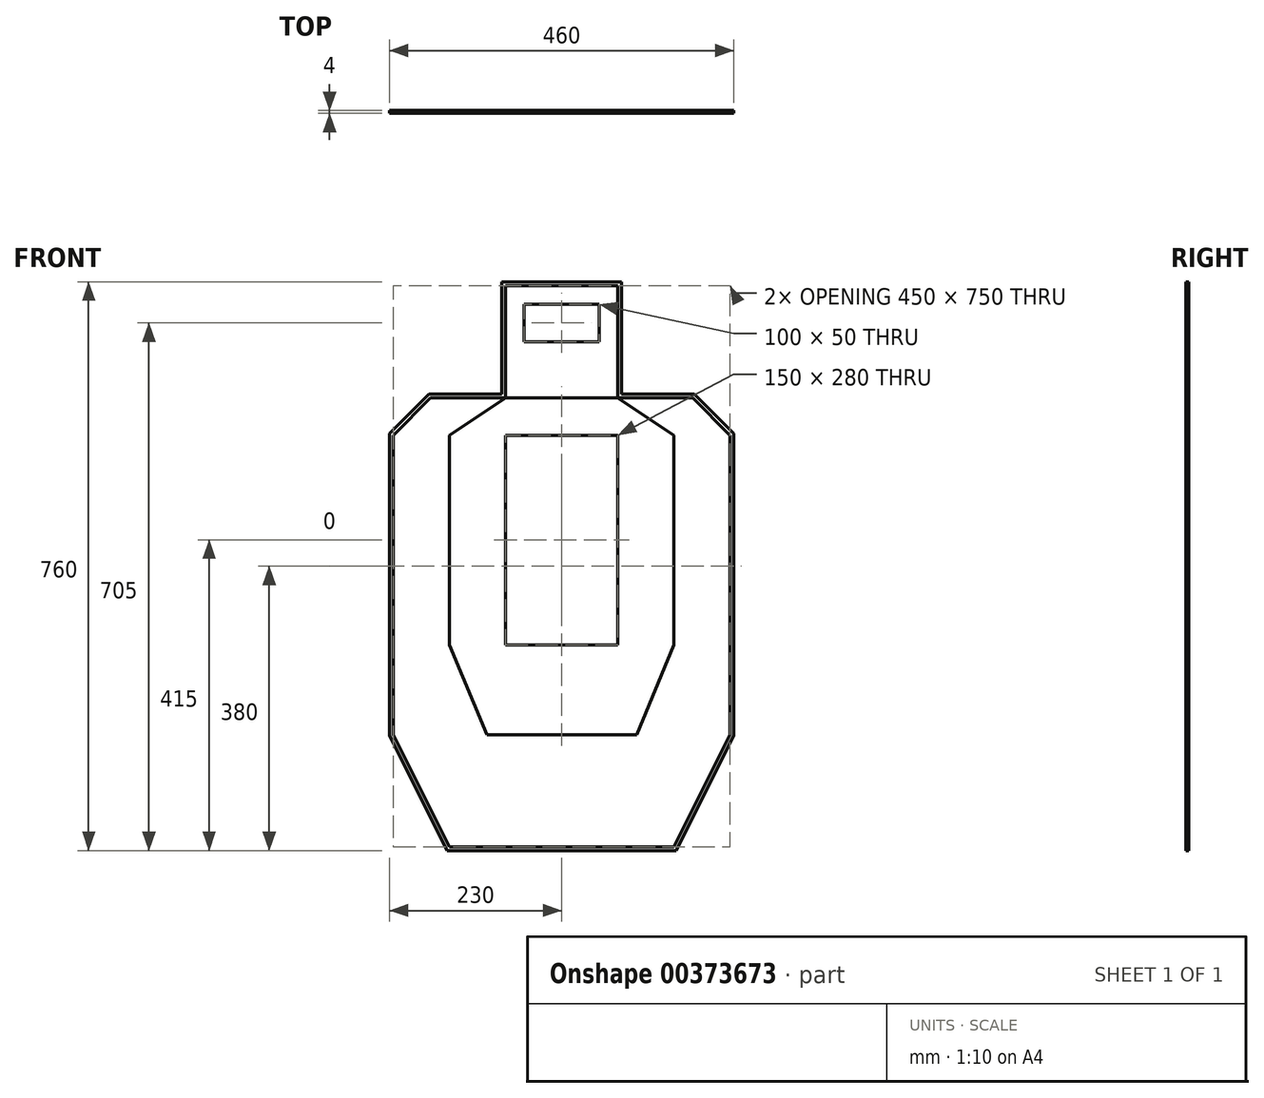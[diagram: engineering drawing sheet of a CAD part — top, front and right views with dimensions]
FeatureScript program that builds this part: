
annotation { "Feature Type Name" : "Feature", "Feature Type Description" : "" }
export const myFeature = defineFeature(function(context is Context, id is Id, definition is map)
    precondition{}
    {
        {
            var Q0;
            Q0=qCreatedBy(makeId("Front.planeOp"),FACE);
            var sketch = newSketch(context, id + "F0", { "sketchPlane" : qUnion([Q0])});
            skLineSegment(sketch, "E0.bottom", {"start": v(0, 100) * mm, "end": v(50, 100) * mm, "construction": true});
            skLineSegment(sketch, "E0.top", {"start": v(0, 125) * mm, "end": v(50, 125) * mm});
            skLineSegment(sketch, "E0.right", {"start": v(50, 100) * mm, "end": v(50, 125) * mm});
            skLineSegment(sketch, "E1.MirrorCS", {"start": v(0, 75) * mm, "end": v(50, 75) * mm});
            skLineSegment(sketch, "E2.MirrorCS", {"start": v(50, 100) * mm, "end": v(50, 75) * mm});
            skLineSegment(sketch, "E3.MirrorCS", {"start": v(0, 0) * mm, "end": v(0, 100) * mm, "construction": true});
            skLineSegment(sketch, "E4.MirrorCS", {"start": v(0, 125) * mm, "end": v(-50, 125) * mm});
            skLineSegment(sketch, "E5.MirrorCS", {"start": v(-50, 100) * mm, "end": v(-50, 125) * mm});
            skLineSegment(sketch, "E6.MirrorCS", {"start": v(-50, 100) * mm, "end": v(-50, 75) * mm});
            skLineSegment(sketch, "E7.MirrorCS", {"start": v(0, 75) * mm, "end": v(-50, 75) * mm});
            skSolve(sketch);
        }
        {
            var Q0;
            Q0 = qSketchRegion(id + "F0", true);
            extrude(context, id + "F1", {"entities" : qUnion([Q0]), "oppositeDirection" : true, "depth" : 3 * mm});
        }
        {
            var Q0;
            Q0=qCreatedBy(makeId("Front.planeOp"),FACE);
            var sketch = newSketch(context, id + "F2", { "sketchPlane" : qUnion([Q0])});
            skLineSegment(sketch, "E8", {"start": v(75, 0) * mm, "end": v(75, 150) * mm});
            skLineSegment(sketch, "E9", {"start": v(75, 150) * mm, "end": v(-75, 150) * mm});
            skLineSegment(sketch, "E10", {"start": v(-75, 150) * mm, "end": v(-75, 0) * mm});
            skLineSegment(sketch, "E11", {"start": v(-75, 0) * mm, "end": v(75, 0) * mm});
            skLineSegment(sketch, "E12.0", {"start": v(0, 125) * mm, "end": v(-50, 125) * mm});
            skLineSegment(sketch, "E13.0", {"start": v(0, 125) * mm, "end": v(50, 125) * mm});
            skLineSegment(sketch, "E14.0", {"start": v(50, 100) * mm, "end": v(50, 125) * mm});
            skLineSegment(sketch, "E15.1", {"start": v(50, 100) * mm, "end": v(50, 75) * mm});
            skLineSegment(sketch, "E16.0", {"start": v(0, 75) * mm, "end": v(50, 75) * mm});
            skLineSegment(sketch, "E17.0", {"start": v(0, 75) * mm, "end": v(-50, 75) * mm});
            skLineSegment(sketch, "E18.0", {"start": v(-50, 100) * mm, "end": v(-50, 75) * mm});
            skLineSegment(sketch, "E19.1", {"start": v(-50, 100) * mm, "end": v(-50, 125) * mm});
            skLineSegment(sketch, "E20", {"start": v(0, 125) * mm, "end": v(0, 150) * mm, "construction": true});
            skLineSegment(sketch, "E21", {"start": v(0, 150) * mm, "end": v(0, 137.5) * mm, "construction": true});
            skSolve(sketch);
        }
        {
            var Q0;
            {var subQ0=sQuery(id+"F2.wireOp",EDGE,"E8");Q0=makeQuery(id+"F2.imprint","IMPRINT",FACE,{"disambiguationData":[TD([[makeQuery(id+"F2.imprint","IMPRINT",EDGE,{"derivedFrom":subQ0}),1.0]])]});}
            extrude(context, id + "F3", {"entities" : qUnion([Q0]), "oppositeDirection" : true, "depth" : 3 * mm});
        }
        {
            var Q0;
            Q0=qCreatedBy(makeId("Front.planeOp"),FACE);
            var sketch = newSketch(context, id + "F4", { "sketchPlane" : qUnion([Q0])});
            skLineSegment(sketch, "E22.bottom", {"start": v(75, -50) * mm, "end": v(-75, -50) * mm});
            skLineSegment(sketch, "E22.top", {"start": v(75, -330) * mm, "end": v(-75, -330) * mm});
            skLineSegment(sketch, "E22.left", {"start": v(75, -50) * mm, "end": v(75, -330) * mm});
            skLineSegment(sketch, "E22.right", {"start": v(-75, -50) * mm, "end": v(-75, -330) * mm});
            skLineSegment(sketch, "E23", {"start": v(0, 0) * mm, "end": v(0, -50) * mm, "construction": true});
            skLineSegment(sketch, "E24.0", {"start": v(-75, 0) * mm, "end": v(75, 0) * mm, "construction": true});
            skLineSegment(sketch, "E25", {"start": v(75, 0) * mm, "end": v(75, -50) * mm, "construction": true});
            skSolve(sketch);
        }
        {
            var Q0;
            Q0=makeQuery(id+"F4.imprint","IMPRINT",FACE,{"disambiguationData":[TD([[makeQuery(id+"F4.imprint","IMPRINT",EDGE,{"derivedFrom":sQuery(id+"F4.wireOp",EDGE,"E22.bottom")}),1.0]])]});
            extrude(context, id + "F5", {"entities" : qUnion([Q0]), "oppositeDirection" : true, "depth" : 3 * mm});
        }
        {
            var Q0;
            Q0=qCreatedBy(makeId("Front.planeOp"),FACE);
            var sketch = newSketch(context, id + "F6", { "sketchPlane" : qUnion([Q0])});
            skLineSegment(sketch, "E26.0", {"start": v(-75, 0) * mm, "end": v(75, 0) * mm});
            skLineSegment(sketch, "E27.1", {"start": v(75, -50) * mm, "end": v(75, -330) * mm});
            skLineSegment(sketch, "E28.2", {"start": v(75, -50) * mm, "end": v(-75, -50) * mm});
            skLineSegment(sketch, "E29.3", {"start": v(-75, -50) * mm, "end": v(-75, -330) * mm});
            skLineSegment(sketch, "E30.0", {"start": v(75, -330) * mm, "end": v(-75, -330) * mm});
            skLineSegment(sketch, "E31", {"start": v(75, 0) * mm, "end": v(150, -50) * mm});
            skLineSegment(sketch, "E32", {"start": v(150, -50) * mm, "end": v(150, -330) * mm});
            skLineSegment(sketch, "E33", {"start": v(150, -330) * mm, "end": v(100, -450) * mm});
            skLineSegment(sketch, "E34", {"start": v(100, -450) * mm, "end": v(-100, -450) * mm});
            skLineSegment(sketch, "E35", {"start": v(-100, -450) * mm, "end": v(-150, -330) * mm});
            skLineSegment(sketch, "E36", {"start": v(-150, -330) * mm, "end": v(-150, -50) * mm});
            skLineSegment(sketch, "E37", {"start": v(-150, -50) * mm, "end": v(-75, 0) * mm});
            skLineSegment(sketch, "E38", {"start": v(0, -450) * mm, "end": v(0, -50) * mm, "construction": true});
            skLineSegment(sketch, "E39", {"start": v(150, -50) * mm, "end": v(75, -50) * mm, "construction": true});
            skLineSegment(sketch, "E40", {"start": v(-55.04, -50) * mm, "end": v(-150, -50) * mm, "construction": true});
            skLineSegment(sketch, "E41", {"start": v(150, -330) * mm, "end": v(150, -450) * mm, "construction": true});
            skLineSegment(sketch, "E42", {"start": v(100, -450) * mm, "end": v(150, -450) * mm, "construction": true});
            skLineSegment(sketch, "E43", {"start": v(150, -330) * mm, "end": v(-150, -330) * mm, "construction": true});
            skLineSegment(sketch, "E44", {"start": v(-150, -330) * mm, "end": v(-150, -450) * mm, "construction": true});
            skLineSegment(sketch, "E45", {"start": v(-150, -450) * mm, "end": v(-100, -450) * mm, "construction": true});
            skSolve(sketch);
        }
        {
            var Q0;
            Q0=makeQuery(id+"F6.imprint","IMPRINT",FACE,{"disambiguationData":[TD([[makeQuery(id+"F6.imprint","IMPRINT",EDGE,{"derivedFrom":sQuery(id+"F6.wireOp",EDGE,"E26.0")}),-1.0]])]});
            extrude(context, id + "F7", {"entities" : qUnion([Q0]), "oppositeDirection" : true, "depth" : 3 * mm});
        }
        {
            var Q0;
            Q0=makeQuery(id+"F7.opExtrude","CAP_FACE",FACE,{"disambiguationData":[OSD([sQuery(id+"F6.wireOp",EDGE,"E26.0"),sQuery(id+"F6.wireOp",EDGE,"E27.1"),sQuery(id+"F6.wireOp",EDGE,"E28.2"),sQuery(id+"F6.wireOp",EDGE,"E29.3"),sQuery(id+"F6.wireOp",EDGE,"E30.0"),sQuery(id+"F6.wireOp",EDGE,"E31"),sQuery(id+"F6.wireOp",EDGE,"E32"),sQuery(id+"F6.wireOp",EDGE,"E33"),sQuery(id+"F6.wireOp",EDGE,"E34"),sQuery(id+"F6.wireOp",EDGE,"E35"),sQuery(id+"F6.wireOp",EDGE,"E36"),sQuery(id+"F6.wireOp",EDGE,"E37")])],"isStart":true});
            var sketch = newSketch(context, id + "F8", { "sketchPlane" : qUnion([Q0])});
            skLineSegment(sketch, "E46.0", {"start": v(75, 0) * mm, "end": v(150, -50) * mm});
            skLineSegment(sketch, "E47.0", {"start": v(150, -50) * mm, "end": v(150, -330) * mm});
            skLineSegment(sketch, "E48.0", {"start": v(150, -330) * mm, "end": v(100, -450) * mm});
            skLineSegment(sketch, "E49.1", {"start": v(100, -450) * mm, "end": v(-100, -450) * mm});
            skLineSegment(sketch, "E50.0", {"start": v(-150, -330) * mm, "end": v(-150, -50) * mm});
            skLineSegment(sketch, "E51.0", {"start": v(-100, -450) * mm, "end": v(-150, -330) * mm});
            skLineSegment(sketch, "E52.0", {"start": v(-150, -50) * mm, "end": v(-75, 0) * mm});
            skLineSegment(sketch, "E53", {"start": v(75, 0) * mm, "end": v(175, 0) * mm});
            skLineSegment(sketch, "E54", {"start": v(175, 0) * mm, "end": v(225, -50) * mm});
            skLineSegment(sketch, "E55", {"start": v(225, -50) * mm, "end": v(225, -450) * mm});
            skLineSegment(sketch, "E56", {"start": v(225, -450) * mm, "end": v(150, -600) * mm});
            skLineSegment(sketch, "E57", {"start": v(150, -600) * mm, "end": v(-150, -600) * mm});
            skLineSegment(sketch, "E58", {"start": v(-150, -600) * mm, "end": v(-225, -450) * mm});
            skLineSegment(sketch, "E59", {"start": v(-225, -450) * mm, "end": v(-225, -50) * mm});
            skLineSegment(sketch, "E60", {"start": v(-225, -50) * mm, "end": v(-175, 0) * mm});
            skLineSegment(sketch, "E61", {"start": v(-175, 0) * mm, "end": v(-75, 0) * mm});
            skLineSegment(sketch, "E62", {"start": v(225, -50) * mm, "end": v(225, 0) * mm, "construction": true});
            skLineSegment(sketch, "E63", {"start": v(225, 0) * mm, "end": v(175, 0) * mm, "construction": true});
            skLineSegment(sketch, "E64", {"start": v(225, -450) * mm, "end": v(225, -600) * mm, "construction": true});
            skLineSegment(sketch, "E65", {"start": v(225, -600) * mm, "end": v(150, -600) * mm, "construction": true});
            skLineSegment(sketch, "E66", {"start": v(-225, -450) * mm, "end": v(-225, -600) * mm, "construction": true});
            skLineSegment(sketch, "E67", {"start": v(-225, -600) * mm, "end": v(-150, -600) * mm, "construction": true});
            skLineSegment(sketch, "E68", {"start": v(-175, 0) * mm, "end": v(-225, 0) * mm, "construction": true});
            skLineSegment(sketch, "E69", {"start": v(-225, 0) * mm, "end": v(-225, -50) * mm, "construction": true});
            skSolve(sketch);
        }
        {
            var Q0;
            Q0 = qSketchRegion(id + "F8", true);
            extrude(context, id + "F9", {"entities" : qUnion([Q0]), "oppositeDirection" : true, "depth" : 3 * mm});
        }
        {
            var Q0;
            Q0=makeQuery(id+"F9.opExtrude","CAP_FACE",FACE,{"disambiguationData":[OSD([sQuery(id+"F8.wireOp",EDGE,"E46.0"),sQuery(id+"F8.wireOp",EDGE,"E47.0"),sQuery(id+"F8.wireOp",EDGE,"E48.0"),sQuery(id+"F8.wireOp",EDGE,"E49.1"),sQuery(id+"F8.wireOp",EDGE,"E50.0"),sQuery(id+"F8.wireOp",EDGE,"E51.0"),sQuery(id+"F8.wireOp",EDGE,"E52.0"),sQuery(id+"F8.wireOp",EDGE,"E53"),sQuery(id+"F8.wireOp",EDGE,"E54"),sQuery(id+"F8.wireOp",EDGE,"E55"),sQuery(id+"F8.wireOp",EDGE,"E56"),sQuery(id+"F8.wireOp",EDGE,"E57"),sQuery(id+"F8.wireOp",EDGE,"E58"),sQuery(id+"F8.wireOp",EDGE,"E59"),sQuery(id+"F8.wireOp",EDGE,"E60"),sQuery(id+"F8.wireOp",EDGE,"E61")])],"isStart":true});
            var sketch = newSketch(context, id + "F10", { "sketchPlane" : qUnion([Q0])});
            skLineSegment(sketch, "E70.0", {"start": v(75, 150) * mm, "end": v(-75, 150) * mm});
            skLineSegment(sketch, "E71.0", {"start": v(75, 0) * mm, "end": v(75, 150) * mm});
            skLineSegment(sketch, "E72.1", {"start": v(75, 0) * mm, "end": v(175, 0) * mm});
            skLineSegment(sketch, "E73.0", {"start": v(175, 0) * mm, "end": v(225, -50) * mm});
            skLineSegment(sketch, "E74.1", {"start": v(225, -50) * mm, "end": v(225, -450) * mm});
            skLineSegment(sketch, "E75.0", {"start": v(225, -450) * mm, "end": v(150, -600) * mm});
            skLineSegment(sketch, "E76.1", {"start": v(150, -600) * mm, "end": v(-150, -600) * mm});
            skLineSegment(sketch, "E77.2", {"start": v(-150, -600) * mm, "end": v(-225, -450) * mm});
            skLineSegment(sketch, "E78.3", {"start": v(-225, -450) * mm, "end": v(-225, -50) * mm});
            skLineSegment(sketch, "E79.4", {"start": v(-225, -50) * mm, "end": v(-175, 0) * mm});
            skLineSegment(sketch, "E80.5", {"start": v(-175, 0) * mm, "end": v(-75, 0) * mm});
            skLineSegment(sketch, "E81.0", {"start": v(-75, 150) * mm, "end": v(-75, 0) * mm});
            skLineSegment(sketch, "E82.0", {"start": v(177.07, 5) * mm, "end": v(230, -47.93) * mm});
            skLineSegment(sketch, "E82.1", {"start": v(-230, -451.18) * mm, "end": v(-230, -47.93) * mm});
            skLineSegment(sketch, "E82.2", {"start": v(-153.1, -605) * mm, "end": v(-230, -451.18) * mm});
            skLineSegment(sketch, "E82.3", {"start": v(153.1, -605) * mm, "end": v(-153.1, -605) * mm});
            skLineSegment(sketch, "E82.4", {"start": v(230, -451.18) * mm, "end": v(153.1, -605) * mm});
            skLineSegment(sketch, "E82.5", {"start": v(-230, -47.93) * mm, "end": v(-177.07, 5) * mm});
            skLineSegment(sketch, "E82.6", {"start": v(230, -47.93) * mm, "end": v(230, -451.18) * mm});
            skLineSegment(sketch, "E82.7", {"start": v(-177.07, 5) * mm, "end": v(-80, 5) * mm});
            skLineSegment(sketch, "E82.8", {"start": v(-80, 155) * mm, "end": v(-80, 5) * mm});
            skLineSegment(sketch, "E82.9", {"start": v(80, 155) * mm, "end": v(-80, 155) * mm});
            skLineSegment(sketch, "E82.10", {"start": v(80, 5) * mm, "end": v(80, 155) * mm});
            skLineSegment(sketch, "E82.11", {"start": v(80, 5) * mm, "end": v(177.07, 5) * mm});
            skSolve(sketch);
        }
        {
            var Q0;
            Q0=makeQuery(id+"F10.imprint","IMPRINT",FACE,{"disambiguationData":[TD([[makeQuery(id+"F10.imprint","IMPRINT",EDGE,{"derivedFrom":sQuery(id+"F10.wireOp",EDGE,"E70.0")}),-1.0]])]});
            extrude(context, id + "F11", {"entities" : qUnion([Q0]), "oppositeDirection" : true, "depth" : 3 * mm});
        }
        {
            var Q0;
            Q0=makeQuery(id+"F9.opExtrude","CAP_FACE",FACE,{"disambiguationData":[OSD([sQuery(id+"F8.wireOp",EDGE,"E46.0"),sQuery(id+"F8.wireOp",EDGE,"E47.0"),sQuery(id+"F8.wireOp",EDGE,"E48.0"),sQuery(id+"F8.wireOp",EDGE,"E49.1"),sQuery(id+"F8.wireOp",EDGE,"E50.0"),sQuery(id+"F8.wireOp",EDGE,"E51.0"),sQuery(id+"F8.wireOp",EDGE,"E52.0"),sQuery(id+"F8.wireOp",EDGE,"E53"),sQuery(id+"F8.wireOp",EDGE,"E54"),sQuery(id+"F8.wireOp",EDGE,"E55"),sQuery(id+"F8.wireOp",EDGE,"E56"),sQuery(id+"F8.wireOp",EDGE,"E57"),sQuery(id+"F8.wireOp",EDGE,"E58"),sQuery(id+"F8.wireOp",EDGE,"E59"),sQuery(id+"F8.wireOp",EDGE,"E60"),sQuery(id+"F8.wireOp",EDGE,"E61")])],"isStart":false});
            var sketch = newSketch(context, id + "F12", { "sketchPlane" : qUnion([Q0])});
            skLineSegment(sketch, "E83.0", {"start": v(75, 150) * mm, "end": v(75, 0) * mm});
            skLineSegment(sketch, "E84.0", {"start": v(175, 0) * mm, "end": v(75, 0) * mm});
            skLineSegment(sketch, "E85.0", {"start": v(-75, 150) * mm, "end": v(75, 150) * mm});
            skLineSegment(sketch, "E86.0", {"start": v(225, -50) * mm, "end": v(175, 0) * mm});
            skLineSegment(sketch, "E87.0", {"start": v(-225, -50) * mm, "end": v(-225, -450) * mm});
            skLineSegment(sketch, "E87.1", {"start": v(225, -450) * mm, "end": v(225, -50) * mm});
            skLineSegment(sketch, "E87.2", {"start": v(150, -600) * mm, "end": v(225, -450) * mm});
            skLineSegment(sketch, "E87.3", {"start": v(-225, -450) * mm, "end": v(-150, -600) * mm});
            skLineSegment(sketch, "E87.4", {"start": v(-150, -600) * mm, "end": v(150, -600) * mm});
            skLineSegment(sketch, "E88.0", {"start": v(-175, 0) * mm, "end": v(-225, -50) * mm});
            skLineSegment(sketch, "E89.0", {"start": v(-75, 0) * mm, "end": v(-175, 0) * mm});
            skLineSegment(sketch, "E90.0", {"start": v(-75, 0) * mm, "end": v(-75, 150) * mm});
            skSolve(sketch);
        }
        {
            var Q0;
            Q0 = qSketchRegion(id + "F12", true);
            extrude(context, id + "F13", {"entities" : qUnion([Q0]), "depth" : 1 * mm});
        }
        {
            var Q0;
            Q0=makeQuery(id+"F13.opExtrude","CAP_FACE",FACE,{"disambiguationData":[OSD([sQuery(id+"F12.wireOp",EDGE,"E83.0"),sQuery(id+"F12.wireOp",EDGE,"E84.0"),sQuery(id+"F12.wireOp",EDGE,"E85.0"),sQuery(id+"F12.wireOp",EDGE,"E86.0"),sQuery(id+"F12.wireOp",EDGE,"E87.0"),sQuery(id+"F12.wireOp",EDGE,"E87.1"),sQuery(id+"F12.wireOp",EDGE,"E87.2"),sQuery(id+"F12.wireOp",EDGE,"E87.3"),sQuery(id+"F12.wireOp",EDGE,"E87.4"),sQuery(id+"F12.wireOp",EDGE,"E88.0"),sQuery(id+"F12.wireOp",EDGE,"E89.0"),sQuery(id+"F12.wireOp",EDGE,"E90.0")])],"isStart":false});
            var sketch = newSketch(context, id + "F14", { "sketchPlane" : qUnion([Q0])});
            skLineSegment(sketch, "E91.0", {"start": v(-80, 155) * mm, "end": v(80, 155) * mm});
            skLineSegment(sketch, "E92.0", {"start": v(80, 155) * mm, "end": v(80, 5) * mm});
            skLineSegment(sketch, "E93.0", {"start": v(-80, 5) * mm, "end": v(-80, 155) * mm});
            skLineSegment(sketch, "E94.0", {"start": v(177.07, 5) * mm, "end": v(80, 5) * mm});
            skLineSegment(sketch, "E95.0", {"start": v(-80, 5) * mm, "end": v(-177.07, 5) * mm});
            skLineSegment(sketch, "E96.0", {"start": v(230, -47.93) * mm, "end": v(177.07, 5) * mm});
            skLineSegment(sketch, "E97.0", {"start": v(-177.07, 5) * mm, "end": v(-230, -47.93) * mm});
            skLineSegment(sketch, "E98.1", {"start": v(-230, -47.93) * mm, "end": v(-230, -451.18) * mm});
            skLineSegment(sketch, "E99.0", {"start": v(-230, -451.18) * mm, "end": v(-153.1, -605) * mm});
            skLineSegment(sketch, "E100.0", {"start": v(-153.1, -605) * mm, "end": v(153.1, -605) * mm});
            skLineSegment(sketch, "E101.0", {"start": v(153.1, -605) * mm, "end": v(230, -451.18) * mm});
            skLineSegment(sketch, "E102.0", {"start": v(230, -451.18) * mm, "end": v(230, -47.93) * mm});
            skLineSegment(sketch, "E103.0", {"start": v(-75, 150) * mm, "end": v(75, 150) * mm});
            skLineSegment(sketch, "E104.0", {"start": v(-75, 0) * mm, "end": v(-75, 150) * mm});
            skLineSegment(sketch, "E105.0", {"start": v(75, 150) * mm, "end": v(75, 0) * mm});
            skLineSegment(sketch, "E106.0", {"start": v(175, 0) * mm, "end": v(75, 0) * mm});
            skLineSegment(sketch, "E107.0", {"start": v(225, -50) * mm, "end": v(175, 0) * mm});
            skLineSegment(sketch, "E108.0", {"start": v(150, -600) * mm, "end": v(225, -450) * mm});
            skLineSegment(sketch, "E109.0", {"start": v(225, -450) * mm, "end": v(225, -50) * mm});
            skLineSegment(sketch, "E110.0", {"start": v(-150, -600) * mm, "end": v(150, -600) * mm});
            skLineSegment(sketch, "E111.0", {"start": v(-225, -450) * mm, "end": v(-150, -600) * mm});
            skLineSegment(sketch, "E112.0", {"start": v(-225, -50) * mm, "end": v(-225, -450) * mm});
            skLineSegment(sketch, "E113.0", {"start": v(-175, 0) * mm, "end": v(-225, -50) * mm});
            skLineSegment(sketch, "E114.0", {"start": v(-75, 0) * mm, "end": v(-175, 0) * mm});
            skSolve(sketch);
        }
        {
            var Q0;
            Q0=makeQuery(id+"F14.imprint","IMPRINT",FACE,{"disambiguationData":[TD([[makeQuery(id+"F14.imprint","IMPRINT",EDGE,{"derivedFrom":sQuery(id+"F14.wireOp",EDGE,"E91.0")}),-1.0]])]});
            extrude(context, id + "F15", {"entities" : qUnion([Q0]), "oppositeDirection" : true, "depth" : 1 * mm});
        }
    });
